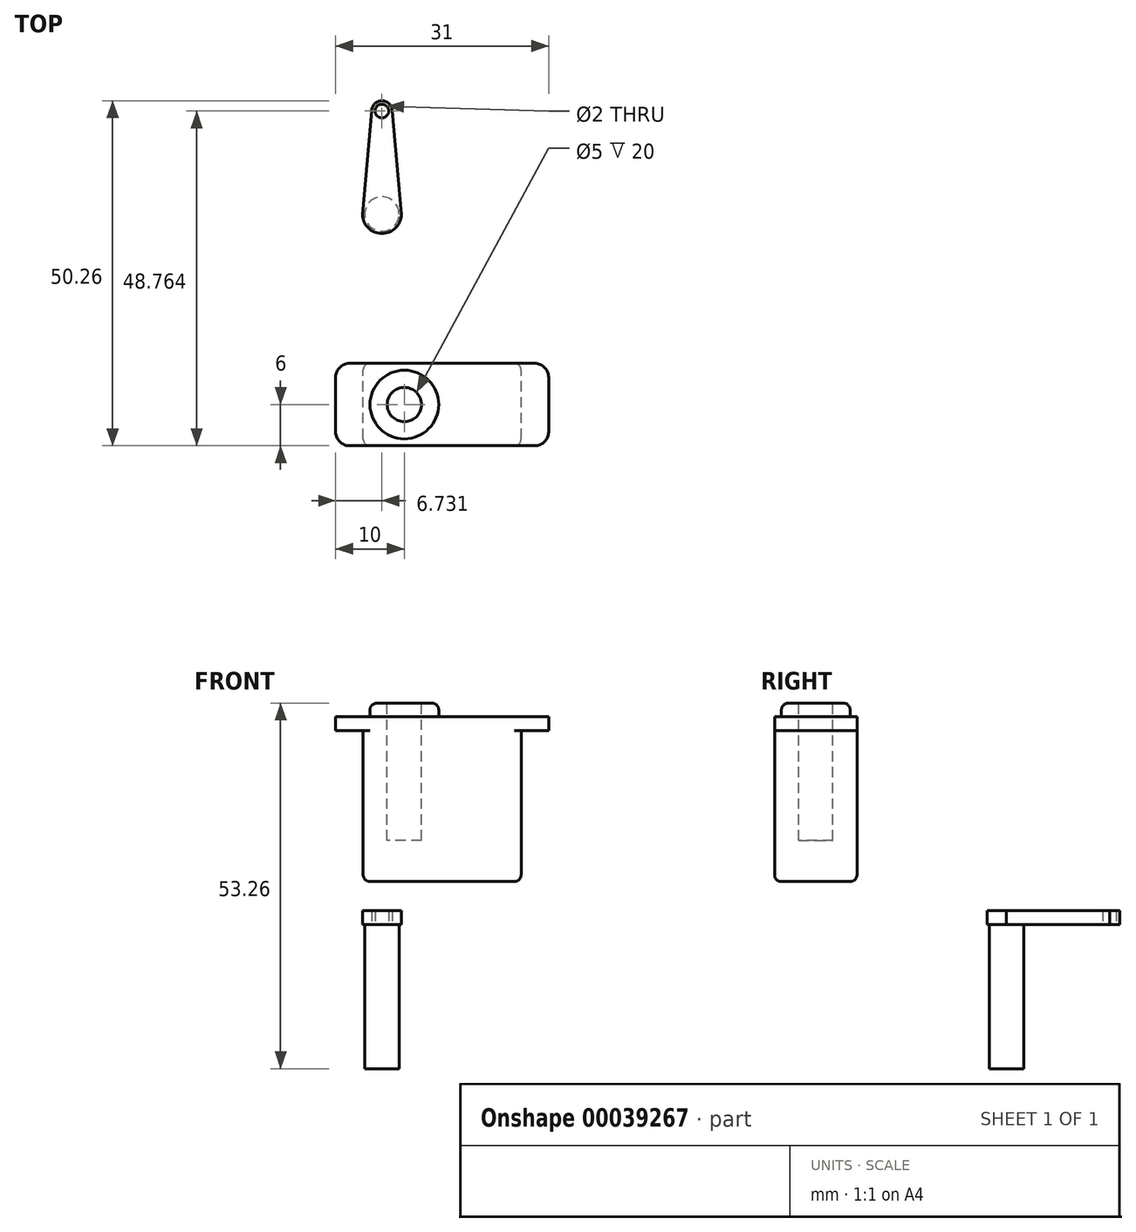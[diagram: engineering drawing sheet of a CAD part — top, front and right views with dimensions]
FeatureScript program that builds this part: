
annotation { "Feature Type Name" : "Feature", "Feature Type Description" : "" }
export const myFeature = defineFeature(function(context is Context, id is Id, definition is map)
    precondition{}
    {
        {
            var Q0;
            Q0=qCreatedBy(makeId("Front.planeOp"),FACE);
            var sketch = newSketch(context, id + "F0", { "sketchPlane" : qUnion([Q0])});
            skLineSegment(sketch, "E0.rect.bottom", {"start": v(-30.23, 27.26) * mm, "end": v(-53.23, 27.26) * mm});
            skLineSegment(sketch, "E0.rect.top", {"start": v(-30.23, 49.26) * mm, "end": v(-53.23, 49.26) * mm});
            skLineSegment(sketch, "E0.rect.left", {"start": v(-30.23, 27.26) * mm, "end": v(-30.23, 49.26) * mm});
            skLineSegment(sketch, "E0.rect.right", {"start": v(-53.23, 27.26) * mm, "end": v(-53.23, 49.26) * mm});
            skPoint(sketch, "E0.rect.middle", {"position": v(-41.73, 38.26) * mm});
            skLineSegment(sketch, "E1", {"start": v(-30.23, 49.26) * mm, "end": v(-26.23, 49.26) * mm});
            skLineSegment(sketch, "E2", {"start": v(-26.23, 49.26) * mm, "end": v(-26.23, 51.26) * mm});
            skLineSegment(sketch, "E3", {"start": v(-26.23, 51.26) * mm, "end": v(-57.23, 51.26) * mm});
            skLineSegment(sketch, "E4", {"start": v(-57.23, 51.26) * mm, "end": v(-57.23, 49.26) * mm});
            skLineSegment(sketch, "E5", {"start": v(-57.23, 49.26) * mm, "end": v(-53.23, 49.26) * mm});
            skSolve(sketch);
        }
        {
            var Q0;
            Q0=makeQuery(id+"F0.imprint","IMPRINT",FACE,{"disambiguationData":[TD([[makeQuery(id+"F0.imprint","IMPRINT",EDGE,{"derivedFrom":sQuery(id+"F0.wireOp",EDGE,"E0.rect.top")}),-1.0]])]});
            var Q1;
            Q1=makeQuery(id+"F0.imprint","IMPRINT",FACE,{"disambiguationData":[TD([[makeQuery(id+"F0.imprint","IMPRINT",EDGE,{"derivedFrom":sQuery(id+"F0.wireOp",EDGE,"E0.rect.bottom")}),-1.0]])]});
            extrude(context, id + "F1", {"entities" : qUnion([Q0, Q1]), "depth" : 12 * mm});
        }
        {
            var Q0;
            Q0=makeQuery(id+"F1.opExtrude","CAP_EDGE",EDGE,{"disambiguationData":[OSD([sQuery(id+"F0.wireOp",EDGE,"E0.rect.right")])],"isStart":false});
            var Q1;
            Q1=makeQuery(id+"F1.opExtrude","CAP_EDGE",EDGE,{"disambiguationData":[OSD([sQuery(id+"F0.wireOp",EDGE,"E0.rect.left")])],"isStart":false});
            var Q2;
            Q2=makeQuery(id+"F1.opExtrude","CAP_EDGE",EDGE,{"disambiguationData":[OSD([sQuery(id+"F0.wireOp",EDGE,"E0.rect.right")])],"isStart":true});
            var Q3;
            Q3=makeQuery(id+"F1.opExtrude","CAP_EDGE",EDGE,{"disambiguationData":[OSD([sQuery(id+"F0.wireOp",EDGE,"E0.rect.left")])],"isStart":true});
            var Q4;
            Q4=makeQuery(id+"F1.opExtrude","CAP_EDGE",EDGE,{"disambiguationData":[OSD([sQuery(id+"F0.wireOp",EDGE,"E0.rect.bottom")])],"isStart":false});
            var Q5;
            Q5=makeQuery(id+"F1.opExtrude","SWEPT_EDGE",EDGE,{"disambiguationData":[OSD([sQuery(id+"F0.wireOp",EDGE,"E0.rect.bottom"),sQuery(id+"F0.wireOp",EDGE,"E0.rect.right")])]});
            var Q6;
            Q6=makeQuery(id+"F1.opExtrude","SWEPT_EDGE",EDGE,{"disambiguationData":[OSD([sQuery(id+"F0.wireOp",EDGE,"E0.rect.bottom"),sQuery(id+"F0.wireOp",EDGE,"E0.rect.left")])]});
            var Q7;
            Q7=makeQuery(id+"F1.opExtrude","CAP_EDGE",EDGE,{"disambiguationData":[OSD([sQuery(id+"F0.wireOp",EDGE,"E0.rect.bottom")])],"isStart":true});
            fillet(context, id + "F2", {"entities" : qUnion([Q0, Q1, Q2, Q3, Q4, Q5, Q6, Q7]), "radius" : 1 * mm, "tangentPropagation" : true, "allowEdgeOverflow" : false});
        }
        {
            var Q0;
            Q0=makeQuery(id+"F1.opExtrude","CAP_EDGE",EDGE,{"disambiguationData":[OSD([sQuery(id+"F0.wireOp",EDGE,"E2")])],"isStart":false});
            var Q1;
            Q1=makeQuery(id+"F1.opExtrude","CAP_EDGE",EDGE,{"disambiguationData":[OSD([sQuery(id+"F0.wireOp",EDGE,"E2")])],"isStart":true});
            var Q2;
            Q2=makeQuery(id+"F1.opExtrude","CAP_EDGE",EDGE,{"disambiguationData":[OSD([sQuery(id+"F0.wireOp",EDGE,"E4")])],"isStart":false});
            var Q3;
            Q3=makeQuery(id+"F1.opExtrude","CAP_EDGE",EDGE,{"disambiguationData":[OSD([sQuery(id+"F0.wireOp",EDGE,"E4")])],"isStart":true});
            fillet(context, id + "F3", {"entities" : qUnion([Q0, Q1, Q2, Q3]), "radius" : 2 * mm, "tangentPropagation" : true, "allowEdgeOverflow" : false});
        }
        {
            var Q0;
            Q0=makeQuery(id+"F1.opExtrude","SWEPT_FACE",FACE,{"disambiguationData":[OSD([sQuery(id+"F0.wireOp",EDGE,"E3")])]});
            var sketch = newSketch(context, id + "F4", { "sketchPlane" : qUnion([Q0])});
            skLineSegment(sketch, "E6", {"start": v(-57.23, -6) * mm, "end": v(-47.23, -6) * mm});
            skCircle(sketch, "E7", {"center": v(-47.23, -6) * mm, "radius": 5 * mm});
            skSolve(sketch);
        }
        {
            var Q0;
            Q0=makeQuery(id+"F4.imprint","IMPRINT",FACE,{"disambiguationData":[TD([[makeQuery(id+"F4.imprint","IMPRINT",EDGE,{"derivedFrom":sQuery(id+"F4.wireOp",EDGE,"E7")}),1.0]])]});
            extrude(context, id + "F5", {"entities" : qUnion([Q0]), "operationType" : NewBodyOperationType.ADD, "depth" : 2 * mm});
        }
        {
            var Q0;
            Q0=makeQuery(id+"F5.opExtrude","CAP_EDGE",EDGE,{"disambiguationData":[OSD([sQuery(id+"F4.wireOp",EDGE,"E7")])],"isStart":false});
            fillet(context, id + "F6", {"entities" : qUnion([Q0]), "radius" : 1 * mm, "tangentPropagation" : true, "allowEdgeOverflow" : false});
        }
        {
            var Q0;
            Q0=makeQuery(id+"F5.opExtrude","CAP_FACE",FACE,{"disambiguationData":[OSD([sQuery(id+"F4.wireOp",EDGE,"E7")])],"isStart":false});
            var sketch = newSketch(context, id + "F7", { "sketchPlane" : qUnion([Q0])});
            skCircle(sketch, "E8", {"center": v(-47.23, -6) * mm, "radius": 2.5 * mm});
            skSolve(sketch);
        }
        {
            var Q0;
            Q0=makeQuery(id+"F7.imprint","IMPRINT",FACE,{"disambiguationData":[TD([[makeQuery(id+"F7.imprint","IMPRINT",EDGE,{"derivedFrom":sQuery(id+"F7.wireOp",EDGE,"E8")}),1.0]])]});
            extrude(context, id + "F8", {"entities" : qUnion([Q0]), "operationType" : NewBodyOperationType.REMOVE, "oppositeDirection" : true, "depth" : 20 * mm});
        }
        {
            var Q0;
            Q0=qCreatedBy(makeId("Top.planeOp"),FACE);
            var sketch = newSketch(context, id + "F9", { "sketchPlane" : qUnion([Q0])});
            skCircle(sketch, "E9", {"center": v(-50.5, 21.76) * mm, "radius": 2.5 * mm});
            skSolve(sketch);
        }
        {
            var Q0;
            Q0=makeQuery(id+"F9.imprint","IMPRINT",FACE,{"disambiguationData":[TD([[makeQuery(id+"F9.imprint","IMPRINT",EDGE,{"derivedFrom":sQuery(id+"F9.wireOp",EDGE,"E9")}),1.0]])]});
            extrude(context, id + "F10", {"entities" : qUnion([Q0]), "depth" : 21 * mm});
        }
        {
            var Q0;
            Q0=makeQuery(id+"F10.opExtrude","CAP_FACE",FACE,{"disambiguationData":[OSD([sQuery(id+"F9.wireOp",EDGE,"E9")])],"isStart":false});
            var sketch = newSketch(context, id + "F11", { "sketchPlane" : qUnion([Q0])});
            skLineSegment(sketch, "E10", {"start": v(-50.5, 21.76) * mm, "end": v(-50.5, 36.76) * mm});
            skCircle(sketch, "E11", {"center": v(-50.5, 21.76) * mm, "radius": 2.83 * mm});
            skCircle(sketch, "E12", {"center": v(-50.5, 36.76) * mm, "radius": 1 * mm});
            skCircle(sketch, "E13", {"center": v(-50.5, 36.76) * mm, "radius": 1.5 * mm});
            skLineSegment(sketch, "E14", {"start": v(-49, 36.76) * mm, "end": v(-47.67, 21.76) * mm});
            skLineSegment(sketch, "E15", {"start": v(-53.33, 21.76) * mm, "end": v(-52, 36.76) * mm});
            skSolve(sketch);
        }
        {
            var Q0;
            {var subQ1=sQuery(id+"F11.wireOp",EDGE,"E11");var subQ5=sQuery(id+"F11.wireOp",EDGE,"E10");var subQ6=makeQuery(id+"F11.imprint","INTERSECT",VERTEX,{"derivedFrom":[subQ5,subQ1]});Q0=makeQuery(id+"F11.imprint","IMPRINT",FACE,{"disambiguationData":[TD([[makeQuery(id+"F11.imprint","IMPRINT",EDGE,{"disambiguationData":[TD([[subQ6,-1.0]])],"derivedFrom":subQ5}),-1.0]])]});}
            var Q1;
            {var subQ0=sQuery(id+"F11.wireOp",EDGE,"E11");var subQ3=sQuery(id+"F11.wireOp",EDGE,"E10");var subQ4=makeQuery(id+"F11.imprint","INTERSECT",VERTEX,{"derivedFrom":[subQ3,subQ0]});Q1=makeQuery(id+"F11.imprint","IMPRINT",FACE,{"disambiguationData":[TD([[makeQuery(id+"F11.imprint","IMPRINT",EDGE,{"disambiguationData":[TD([[subQ4,-1.0]])],"derivedFrom":subQ3}),1.0]])]});}
            var Q2;
            Q2=makeQuery(id+"F11.imprint","IMPRINT",FACE,{"disambiguationData":[TD([[makeQuery(id+"F11.imprint","IMPRINT",EDGE,{"derivedFrom":makeQuery(id+"F10.opExtrude","CAP_EDGE",EDGE,{"disambiguationData":[OSD([sQuery(id+"F9.wireOp",EDGE,"E9")])],"isStart":false})}),-1.0]])]});
            var Q3;
            Q3=makeQuery(id+"F11.imprint","IMPRINT",FACE,{"disambiguationData":[TD([[makeQuery(id+"F11.imprint","IMPRINT",EDGE,{"derivedFrom":makeQuery(id+"F10.opExtrude","CAP_EDGE",EDGE,{"disambiguationData":[OSD([sQuery(id+"F9.wireOp",EDGE,"E9")])],"isStart":false})}),1.0]])]});
            var Q4;
            Q4=makeQuery(id+"F11.imprint","IMPRINT",FACE,{"disambiguationData":[TD([[makeQuery(id+"F11.imprint","IMPRINT",EDGE,{"derivedFrom":sQuery(id+"F11.wireOp",EDGE,"E12")}),-1.0]])]});
            extrude(context, id + "F12", {"entities" : qUnion([Q0, Q1, Q2, Q3, Q4]), "operationType" : NewBodyOperationType.ADD, "depth" : 2 * mm});
        }
    });
